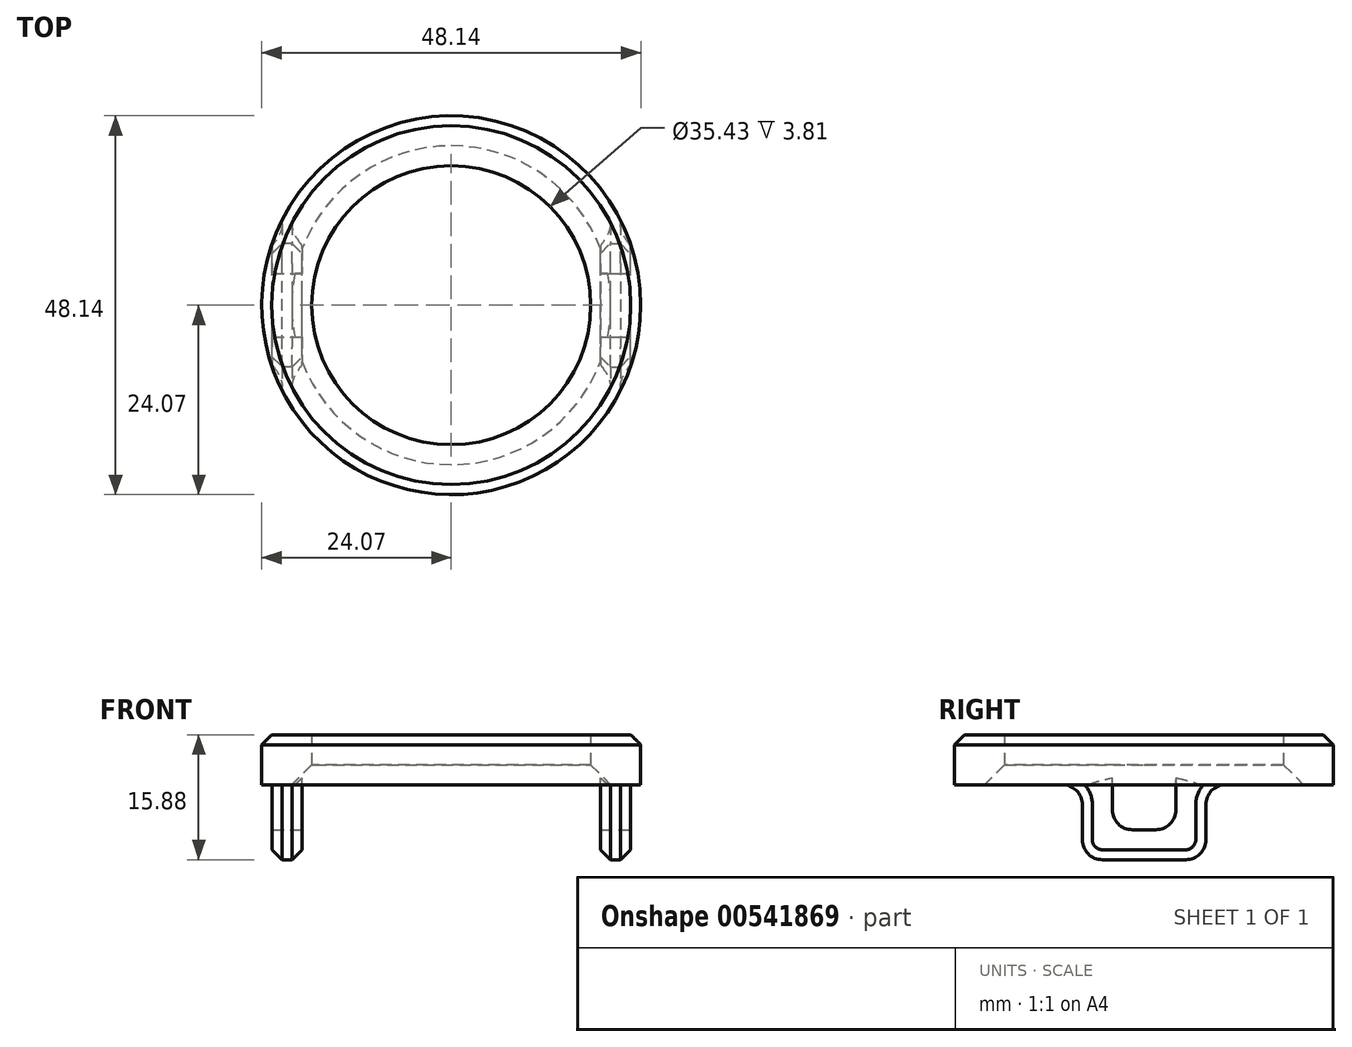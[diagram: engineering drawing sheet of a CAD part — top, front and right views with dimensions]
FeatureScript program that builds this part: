
annotation { "Feature Type Name" : "Feature", "Feature Type Description" : "" }
export const myFeature = defineFeature(function(context is Context, id is Id, definition is map)
    precondition{}
    {
        {
            var Q0;
            Q0=qCreatedBy(makeId("Top.planeOp"),FACE);
            var sketch = newSketch(context, id + "F0", { "sketchPlane" : qUnion([Q0])});
            skCircle(sketch, "E0", {"center": v(0, 0) * mm, "radius": 17.72 * mm});
            skCircle(sketch, "E1.0", {"center": v(0, 0) * mm, "radius": 24.07 * mm});
            skSolve(sketch);
        }
        {
            var Q0;
            Q0=makeQuery(id+"F0.imprint","IMPRINT",FACE,{"disambiguationData":[TD([[makeQuery(id+"F0.imprint","IMPRINT",EDGE,{"derivedFrom":sQuery(id+"F0.wireOp",EDGE,"E0")}),-1.0]])]});
            extrude(context, id + "F1", {"entities" : qUnion([Q0]), "depth" : 6.35 * mm, "offsetDistance" : 25.4 * mm});
        }
        {
            var Q0;
            Q0=makeQuery(id+"F1.opExtrude","CAP_FACE",FACE,{"disambiguationData":[OSD([sQuery(id+"F0.wireOp",EDGE,"E0"),sQuery(id+"F0.wireOp",EDGE,"E1.0")])],"isStart":true});
            var sketch = newSketch(context, id + "F2", { "sketchPlane" : qUnion([Q0])});
            skLineSegment(sketch, "E2.bottom", {"start": v(18.94, 7.84) * mm, "end": v(22.75, 7.84) * mm});
            skLineSegment(sketch, "E2.top", {"start": v(18.94, -7.84) * mm, "end": v(22.75, -7.84) * mm});
            skLineSegment(sketch, "E2.left", {"start": v(18.94, 7.84) * mm, "end": v(18.94, -7.84) * mm});
            skLineSegment(sketch, "E2.right", {"start": v(22.75, 7.84) * mm, "end": v(22.75, -7.84) * mm});
            skLineSegment(sketch, "E3.MirrorCS", {"start": v(-18.94, 7.84) * mm, "end": v(-22.75, 7.84) * mm});
            skLineSegment(sketch, "E4.MirrorCS", {"start": v(-18.94, -7.84) * mm, "end": v(-22.75, -7.84) * mm});
            skLineSegment(sketch, "E5.MirrorCS", {"start": v(-22.75, 7.84) * mm, "end": v(-22.75, -7.84) * mm});
            skLineSegment(sketch, "E6.MirrorCS", {"start": v(-18.94, 7.84) * mm, "end": v(-18.94, -7.84) * mm});
            skSolve(sketch);
        }
        {
            var Q0;
            {var subQ1=sQuery(id+"F2.wireOp",EDGE,"E3.MirrorCS");Q0=makeQuery(id+"F2.imprint","IMPRINT",FACE,{"disambiguationData":[TD([[makeQuery(id+"F2.imprint","IMPRINT",EDGE,{"derivedFrom":subQ1}),1.0]])]});}
            var Q1;
            {var subQ3=sQuery(id+"F2.wireOp",EDGE,"E2.bottom");Q1=makeQuery(id+"F2.imprint","IMPRINT",FACE,{"disambiguationData":[TD([[makeQuery(id+"F2.imprint","IMPRINT",EDGE,{"derivedFrom":subQ3}),-1.0]])]});}
            extrude(context, id + "F3", {"entities" : qUnion([Q0, Q1]), "operationType" : NewBodyOperationType.ADD, "depth" : 9.52 * mm, "offsetDistance" : 25.4 * mm});
        }
        {
            var Q0;
            Q0=makeQuery(id+"F3.opExtrude","SWEPT_FACE",FACE,{"disambiguationData":[OSD([sQuery(id+"F2.wireOp",EDGE,"E2.right")])]});
            var sketch = newSketch(context, id + "F4", { "sketchPlane" : qUnion([Q0])});
            skLineSegment(sketch, "E7.0", {"start": v(4.03, -5.72) * mm, "end": v(4.03, 0) * mm});
            skLineSegment(sketch, "E7.1", {"start": v(-4.03, -5.72) * mm, "end": v(4.03, -5.72) * mm});
            skLineSegment(sketch, "E7.2", {"start": v(-4.03, -5.72) * mm, "end": v(-4.03, 0) * mm});
            skSolve(sketch);
        }
        {
            var Q0;
            {var subQ0=sQuery(id+"F4.wireOp",EDGE,"E7.0");Q0=makeQuery(id+"F4.imprint","IMPRINT",FACE,{"disambiguationData":[TD([[makeQuery(id+"F4.imprint","IMPRINT",EDGE,{"derivedFrom":subQ0}),1.0]])]});}
            extrude(context, id + "F5", {"entities" : qUnion([Q0]), "operationType" : NewBodyOperationType.REMOVE, "endBound" : BoundingType.THROUGH_ALL, "oppositeDirection" : true, "depth" : 25.4 * mm, "offsetDistance" : 25.4 * mm});
        }
        {
            var Q0;
            {var subQ0=makeQuery(id+"F1.opExtrude","CAP_EDGE",EDGE,{"disambiguationData":[OSD([sQuery(id+"F0.wireOp",EDGE,"E0")])],"isStart":true});Q0=makeQuery(id+"F5.boolean.opBoolean","MERGE",EDGE,{"derivedFrom":[makeQuery(id+"F3.boolean.opBoolean","SPLIT",EDGE,{"disambiguationData":[OD(0.0)],"derivedFrom":subQ0}),makeQuery(id+"F3.boolean.opBoolean","SPLIT",EDGE,{"disambiguationData":[OD(1.0)],"derivedFrom":subQ0})]});}
            chamfer(context, id + "F6", {"entities" : qUnion([Q0]), "width" : 2.54 * mm, "tangentPropagation" : true});
        }
        {
            var Q0;
            Q0=makeQuery(id+"F3.opExtrude","CAP_EDGE",EDGE,{"disambiguationData":[OSD([sQuery(id+"F2.wireOp",EDGE,"E2.bottom")])],"isStart":true});
            var Q1;
            Q1=makeQuery(id+"F3.opExtrude","CAP_EDGE",EDGE,{"disambiguationData":[OSD([sQuery(id+"F2.wireOp",EDGE,"E2.top")])],"isStart":true});
            var Q2;
            Q2=makeQuery(id+"F3.opExtrude","CAP_EDGE",EDGE,{"disambiguationData":[OSD([sQuery(id+"F2.wireOp",EDGE,"E4.MirrorCS")])],"isStart":true});
            var Q3;
            Q3=makeQuery(id+"F3.opExtrude","CAP_EDGE",EDGE,{"disambiguationData":[OSD([sQuery(id+"F2.wireOp",EDGE,"E3.MirrorCS")])],"isStart":true});
            var Q4;
            Q4=makeQuery(id+"F3.opExtrude","CAP_EDGE",EDGE,{"disambiguationData":[OSD([sQuery(id+"F2.wireOp",EDGE,"E2.bottom")])],"isStart":false});
            var Q5;
            Q5=makeQuery(id+"F3.opExtrude","CAP_EDGE",EDGE,{"disambiguationData":[OSD([sQuery(id+"F2.wireOp",EDGE,"E2.top")])],"isStart":false});
            var Q6;
            Q6=makeQuery(id+"F3.opExtrude","CAP_EDGE",EDGE,{"disambiguationData":[OSD([sQuery(id+"F2.wireOp",EDGE,"E4.MirrorCS")])],"isStart":false});
            var Q7;
            Q7=makeQuery(id+"F3.opExtrude","CAP_EDGE",EDGE,{"disambiguationData":[OSD([sQuery(id+"F2.wireOp",EDGE,"E3.MirrorCS")])],"isStart":false});
            var Q8;
            {var subQ0=sQuery(id+"F4.wireOp",EDGE,"E7.0");var subQ1=sQuery(id+"F4.wireOp",EDGE,"E7.1");Q8=makeQuery(id+"F5.boolean.opBoolean","COPY",EDGE,{"disambiguationData":[TD([makeQuery(id+"F3.opExtrude","SWEPT_FACE",FACE,{"disambiguationData":[OSD([sQuery(id+"F2.wireOp",EDGE,"E2.left")])]})])],"derivedFrom":makeQuery(id+"F5.opExtrude","SWEPT_EDGE",EDGE,{"disambiguationData":[OSD([subQ0,subQ1])]})});}
            var Q9;
            {var subQ0=sQuery(id+"F4.wireOp",EDGE,"E7.1");var subQ1=sQuery(id+"F4.wireOp",EDGE,"E7.2");Q9=makeQuery(id+"F5.boolean.opBoolean","COPY",EDGE,{"disambiguationData":[TD([makeQuery(id+"F3.opExtrude","SWEPT_FACE",FACE,{"disambiguationData":[OSD([sQuery(id+"F2.wireOp",EDGE,"E2.left")])]})])],"derivedFrom":makeQuery(id+"F5.opExtrude","SWEPT_EDGE",EDGE,{"disambiguationData":[OSD([subQ0,subQ1])]})});}
            var Q10;
            {var subQ0=sQuery(id+"F4.wireOp",EDGE,"E7.0");var subQ1=sQuery(id+"F4.wireOp",EDGE,"E7.1");Q10=makeQuery(id+"F5.boolean.opBoolean","COPY",EDGE,{"disambiguationData":[TD([makeQuery(id+"F3.opExtrude","SWEPT_FACE",FACE,{"disambiguationData":[OSD([sQuery(id+"F2.wireOp",EDGE,"E5.MirrorCS")])]})])],"derivedFrom":makeQuery(id+"F5.opExtrude","SWEPT_EDGE",EDGE,{"disambiguationData":[OSD([subQ0,subQ1])]})});}
            var Q11;
            {var subQ0=sQuery(id+"F4.wireOp",EDGE,"E7.1");var subQ1=sQuery(id+"F4.wireOp",EDGE,"E7.2");Q11=makeQuery(id+"F5.boolean.opBoolean","COPY",EDGE,{"disambiguationData":[TD([makeQuery(id+"F3.opExtrude","SWEPT_FACE",FACE,{"disambiguationData":[OSD([sQuery(id+"F2.wireOp",EDGE,"E5.MirrorCS")])]})])],"derivedFrom":makeQuery(id+"F5.opExtrude","SWEPT_EDGE",EDGE,{"disambiguationData":[OSD([subQ0,subQ1])]})});}
            fillet(context, id + "F7", {"entities" : qUnion([Q0, Q1, Q2, Q3, Q4, Q5, Q6, Q7, Q8, Q9, Q10, Q11]), "radius" : 2.54 * mm, "tangentPropagation" : true, "allowEdgeOverflow" : false});
        }
        {
            var Q0;
            Q0=makeQuery(id+"F1.opExtrude","CAP_EDGE",EDGE,{"disambiguationData":[OSD([sQuery(id+"F0.wireOp",EDGE,"E1.0")])],"isStart":false});
            var Q1;
            Q1=makeQuery(id+"F3.opExtrude","CAP_EDGE",EDGE,{"disambiguationData":[OSD([sQuery(id+"F2.wireOp",EDGE,"E5.MirrorCS")])],"isStart":false});
            var Q2;
            Q2=makeQuery(id+"F3.opExtrude","CAP_EDGE",EDGE,{"disambiguationData":[OSD([sQuery(id+"F2.wireOp",EDGE,"E2.left")])],"isStart":false});
            var Q3;
            Q3=makeQuery(id+"F3.opExtrude","CAP_EDGE",EDGE,{"disambiguationData":[OSD([sQuery(id+"F2.wireOp",EDGE,"E2.right")])],"isStart":false});
            var Q4;
            Q4=makeQuery(id+"F3.opExtrude","CAP_EDGE",EDGE,{"disambiguationData":[OSD([sQuery(id+"F2.wireOp",EDGE,"E6.MirrorCS")])],"isStart":false});
            chamfer(context, id + "F8", {"entities" : qUnion([Q0, Q1, Q2, Q3, Q4]), "width" : 1.27 * mm, "tangentPropagation" : true});
        }
    });
